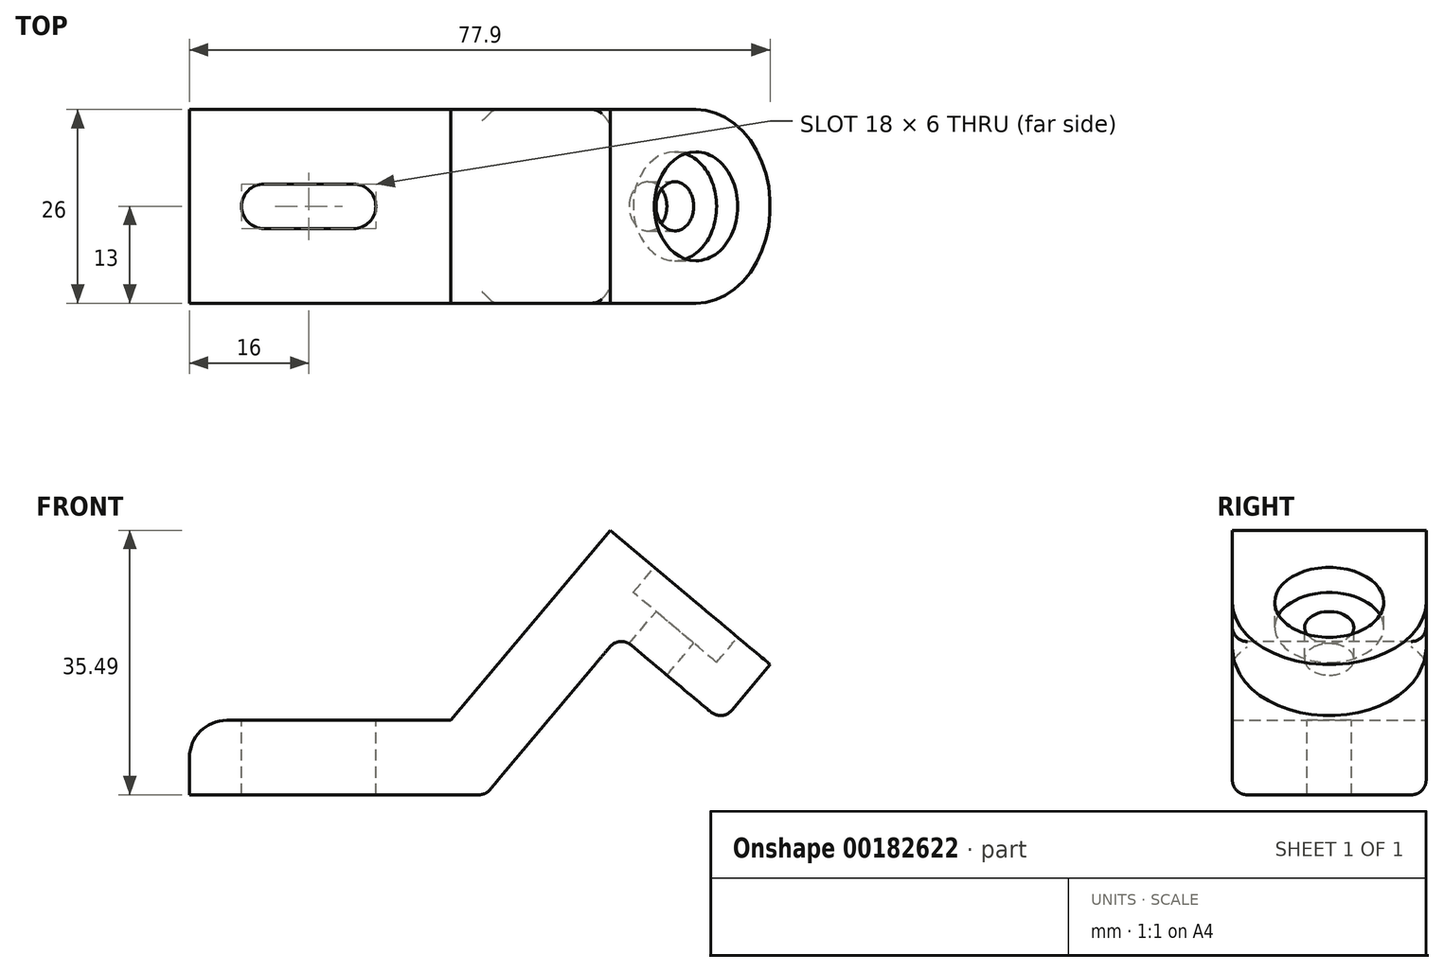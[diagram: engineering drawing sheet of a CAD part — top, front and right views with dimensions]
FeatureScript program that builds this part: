
annotation { "Feature Type Name" : "Feature", "Feature Type Description" : "" }
export const myFeature = defineFeature(function(context is Context, id is Id, definition is map)
    precondition{}
    {
        {
            var Q0;
            Q0=qCreatedBy(makeId("Front.planeOp"),FACE);
            var sketch = newSketch(context, id + "F0", { "sketchPlane" : qUnion([Q0])});
            skLineSegment(sketch, "E0", {"start": v(-38.8, 0) * mm, "end": v(0, 0) * mm});
            skLineSegment(sketch, "E1", {"start": v(0, 0) * mm, "end": v(18.64, 22.22) * mm});
            skLineSegment(sketch, "E2", {"start": v(18.64, 22.22) * mm, "end": v(33.96, 9.36) * mm});
            skLineSegment(sketch, "E3.0", {"start": v(17.65, 33.49) * mm, "end": v(39.1, 15.49) * mm});
            skLineSegment(sketch, "E3.1", {"start": v(-3.73, 8) * mm, "end": v(17.65, 33.49) * mm});
            skLineSegment(sketch, "E3.2", {"start": v(-38.8, 8) * mm, "end": v(-3.73, 8) * mm});
            skLineSegment(sketch, "E4.0", {"start": v(18.89, 19.4) * mm, "end": v(32.68, 7.83) * mm});
            skLineSegment(sketch, "E4.1", {"start": v(0.93, -2) * mm, "end": v(18.89, 19.4) * mm});
            skLineSegment(sketch, "E4.2", {"start": v(-38.8, -2) * mm, "end": v(0.93, -2) * mm});
            skLineSegment(sketch, "E5", {"start": v(-38.8, 8) * mm, "end": v(-38.8, -2) * mm});
            skLineSegment(sketch, "E6", {"start": v(39.1, 15.49) * mm, "end": v(32.68, 7.83) * mm});
            skSolve(sketch);
        }
        {
            var Q0;
            Q0=qSketchRegion(id+"F0",true);
            extrude(context, id + "F1", {"entities" : qUnion([Q0]), "endBound" : BoundingType.SYMMETRIC, "depth" : 26 * mm});
        }
        {
            var Q0;
            Q0=makeQuery(id+"F1.opExtrude","CAP_EDGE",EDGE,{"disambiguationData":[OSD([sQuery(id+"F0.wireOp",EDGE,"E6")])],"isStart":false});
            var Q1;
            Q1=makeQuery(id+"F1.opExtrude","CAP_EDGE",EDGE,{"disambiguationData":[OSD([sQuery(id+"F0.wireOp",EDGE,"E6")])],"isStart":true});
            fillet(context, id + "F2", {"entities" : qUnion([Q0, Q1]), "radius" : 13 * mm, "tangentPropagation" : true, "allowEdgeOverflow" : false});
        }
        {
            var Q0;
            Q0=makeQuery(id+"F1.opExtrude","SWEPT_FACE",FACE,{"disambiguationData":[OSD([sQuery(id+"F0.wireOp",EDGE,"E4.0")])]});
            var Q1;
            Q1=makeQuery(id+"F1.opExtrude","SWEPT_EDGE",EDGE,{"disambiguationData":[OSD([sQuery(id+"F0.wireOp",EDGE,"E4.1"),sQuery(id+"F0.wireOp",EDGE,"E4.2")])]});
            var Q2;
            Q2=makeQuery(id+"F1.opExtrude","CAP_EDGE",EDGE,{"disambiguationData":[OSD([sQuery(id+"F0.wireOp",EDGE,"E4.2")])],"isStart":false});
            var Q3;
            Q3=makeQuery(id+"F1.opExtrude","CAP_EDGE",EDGE,{"disambiguationData":[OSD([sQuery(id+"F0.wireOp",EDGE,"E4.2")])],"isStart":true});
            fillet(context, id + "F3", {"entities" : qUnion([Q0, Q1, Q2, Q3]), "radius" : 2 * mm, "tangentPropagation" : true, "allowEdgeOverflow" : false});
        }
        {
            var Q0;
            Q0=makeQuery(id+"F1.opExtrude","SWEPT_FACE",FACE,{"disambiguationData":[OSD([sQuery(id+"F0.wireOp",EDGE,"E3.0")])]});
            var sketch = newSketch(context, id + "F4", { "sketchPlane" : qUnion([Q0])});
            skCircle(sketch, "E7", {"center": v(7, 0) * mm, "radius": 7.3 * mm});
            skSolve(sketch);
        }
        {
            var Q0;
            Q0=qSketchRegion(id+"F4",true);
            extrude(context, id + "F5", {"entities" : qUnion([Q0]), "operationType" : NewBodyOperationType.REMOVE, "oppositeDirection" : true, "depth" : 4.4 * mm});
        }
        {
            var Q0;
            Q0=makeQuery(id+"F5.boolean.opBoolean","COPY",FACE,{"derivedFrom":makeQuery(id+"F5.opExtrude","CAP_FACE",FACE,{"disambiguationData":[OSD([sQuery(id+"F4.wireOp",EDGE,"E7")])],"isStart":false})});
            var sketch = newSketch(context, id + "F6", { "sketchPlane" : qUnion([Q0])});
            skCircle(sketch, "E8", {"center": v(7, 0) * mm, "radius": 3.3 * mm});
            skSolve(sketch);
        }
        {
            var Q0;
            Q0=qSketchRegion(id+"F6",true);
            extrude(context, id + "F7", {"entities" : qUnion([Q0]), "operationType" : NewBodyOperationType.REMOVE, "endBound" : BoundingType.THROUGH_ALL, "oppositeDirection" : true, "depth" : 25 * mm});
        }
        {
            var Q0;
            Q0=makeQuery(id+"F1.opExtrude","SWEPT_FACE",FACE,{"disambiguationData":[OSD([sQuery(id+"F0.wireOp",EDGE,"E3.2")])]});
            var sketch = newSketch(context, id + "F8", { "sketchPlane" : qUnion([Q0])});
            skLineSegment(sketch, "E9", {"start": v(-28.8, 0) * mm, "end": v(-16.8, 0) * mm});
            skArc(sketch, "E10.0.startCap", {"start": v(-28.8, -3) * mm, "mid": v(-31.8, 0) * mm, "end": v(-28.8, 3) * mm});
            skArc(sketch, "E10.0.endCap", {"start": v(-16.8, 3) * mm, "mid": v(-13.8, 0) * mm, "end": v(-16.8, -3) * mm});
            skLineSegment(sketch, "E10.0.left", {"start": v(-28.8, 3) * mm, "end": v(-16.8, 3) * mm});
            skLineSegment(sketch, "E10.0.right", {"start": v(-28.8, -3) * mm, "end": v(-16.8, -3) * mm});
            skSolve(sketch);
        }
        {
            var Q0;
            Q0=qSketchRegion(id+"F8",true);
            extrude(context, id + "F9", {"entities" : qUnion([Q0]), "operationType" : NewBodyOperationType.REMOVE, "endBound" : BoundingType.THROUGH_ALL, "oppositeDirection" : true, "depth" : 25 * mm});
        }
        {
            var Q0;
            Q0=makeQuery(id+"F1.opExtrude","SWEPT_EDGE",EDGE,{"disambiguationData":[OSD([sQuery(id+"F0.wireOp",EDGE,"E3.2"),sQuery(id+"F0.wireOp",EDGE,"E5")])]});
            fillet(context, id + "F10", {"entities" : qUnion([Q0]), "radius" : 5 * mm, "tangentPropagation" : true, "allowEdgeOverflow" : false});
        }
    });
